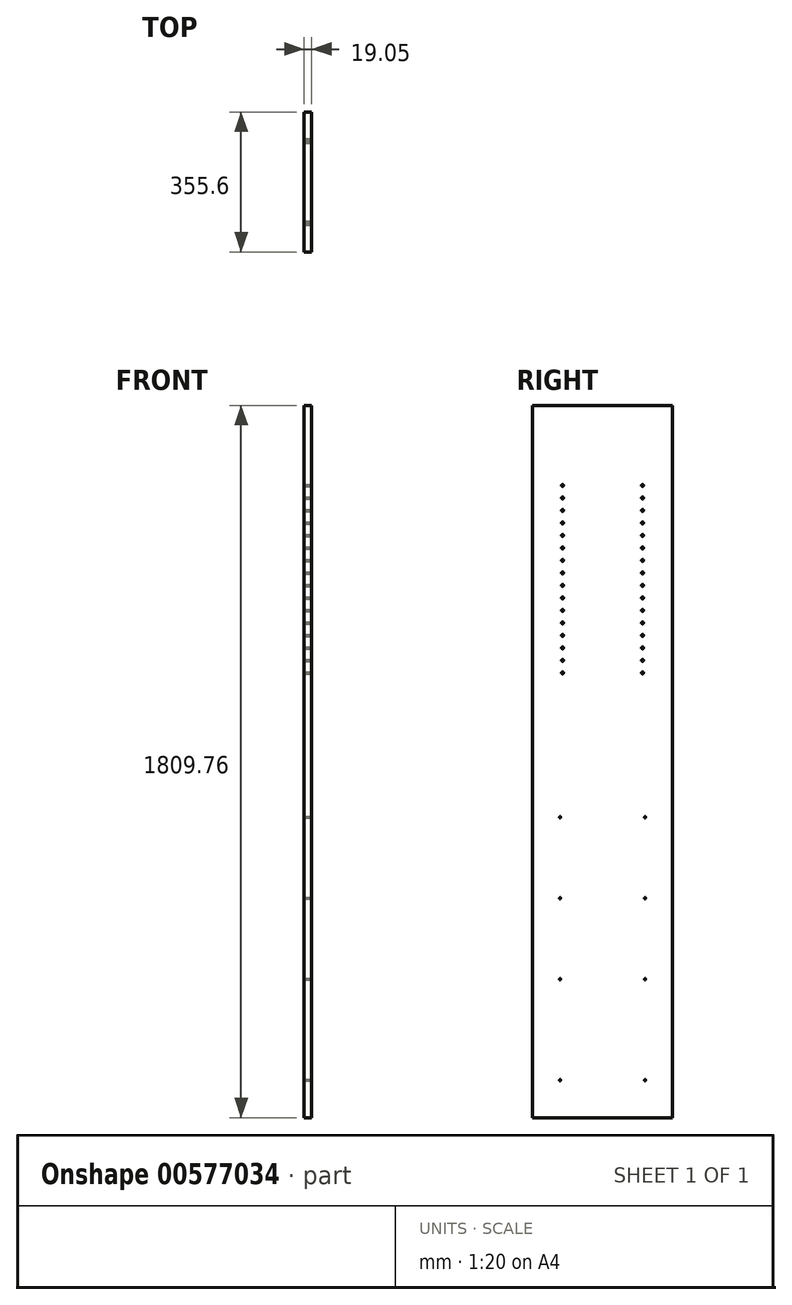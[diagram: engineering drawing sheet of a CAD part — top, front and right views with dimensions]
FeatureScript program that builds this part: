
annotation { "Feature Type Name" : "Feature", "Feature Type Description" : "" }
export const myFeature = defineFeature(function(context is Context, id is Id, definition is map)
    precondition{}
    {
        {
            var Q0;
            Q0=qCreatedBy(makeId("Right.planeOp"),FACE);
            var sketch = newSketch(context, id + "F0", { "sketchPlane" : qUnion([Q0])});
            skLineSegment(sketch, "E0.bottom", {"start": v(177.8, 904.88) * mm, "end": v(-177.8, 904.88) * mm});
            skLineSegment(sketch, "E0.top", {"start": v(177.8, -904.88) * mm, "end": v(-177.8, -904.88) * mm});
            skLineSegment(sketch, "E0.left", {"start": v(177.8, 904.88) * mm, "end": v(177.8, -904.88) * mm});
            skLineSegment(sketch, "E0.right", {"start": v(-177.8, 904.88) * mm, "end": v(-177.8, -904.88) * mm});
            skPoint(sketch, "E0.middle", {"position": v(0, 0) * mm});
            skSolve(sketch);
        }
        {
            var Q0;
            Q0=makeQuery(id+"F0.imprint","IMPRINT",FACE,{"disambiguationData":[TD([[makeQuery(id+"F0.imprint","IMPRINT",EDGE,{"derivedFrom":sQuery(id+"F0.wireOp",EDGE,"E0.bottom")}),1.0]])]});
            extrude(context, id + "F1", {"entities" : qUnion([Q0]), "depth" : 19.05 * mm, "offsetDistance" : 25.4 * mm});
        }
        {
            var Q0;
            Q0=makeQuery(id+"F1.opExtrude","CAP_FACE",FACE,{"disambiguationData":[OSD([sQuery(id+"F0.wireOp",EDGE,"E0.bottom"),sQuery(id+"F0.wireOp",EDGE,"E0.top"),sQuery(id+"F0.wireOp",EDGE,"E0.left"),sQuery(id+"F0.wireOp",EDGE,"E0.right")])],"isStart":false});
            var sketch = newSketch(context, id + "F2", { "sketchPlane" : qUnion([Q0])});
            skLineSegment(sketch, "E1", {"start": v(0, -904.88) * mm, "end": v(0, 9.53) * mm});
            skPoint(sketch, "E1.endSnap0", {"position": v(0, -904.88) * mm});
            skLineSegment(sketch, "E2", {"start": v(0, 904.88) * mm, "end": v(0, 669.92) * mm});
            skLineSegment(sketch, "E3.bottom", {"start": v(101.6, 701.68) * mm, "end": v(-101.6, 701.68) * mm});
            skLineSegment(sketch, "E3.top", {"start": v(101.6, 638.18) * mm, "end": v(-101.6, 638.18) * mm});
            skLineSegment(sketch, "E3.left", {"start": v(101.6, 701.68) * mm, "end": v(101.6, 638.18) * mm});
            skLineSegment(sketch, "E3.right", {"start": v(-101.6, 701.68) * mm, "end": v(-101.6, 638.18) * mm});
            skPoint(sketch, "E3.middle", {"position": v(0, 669.92) * mm});
            skLineSegment(sketch, "E4", {"start": v(0, 638.18) * mm, "end": v(0, 574.68) * mm});
            skLineSegment(sketch, "E5.bottom", {"start": v(-101.6, 542.93) * mm, "end": v(101.6, 542.93) * mm});
            skLineSegment(sketch, "E5.top", {"start": v(-101.6, 606.43) * mm, "end": v(101.6, 606.43) * mm});
            skLineSegment(sketch, "E5.left", {"start": v(-101.6, 542.93) * mm, "end": v(-101.6, 606.43) * mm});
            skLineSegment(sketch, "E5.right", {"start": v(101.6, 542.93) * mm, "end": v(101.6, 606.43) * mm});
            skPoint(sketch, "E5.middle", {"position": v(0, 574.68) * mm});
            skLineSegment(sketch, "E6", {"start": v(0, 542.93) * mm, "end": v(0, 479.43) * mm});
            skLineSegment(sketch, "E7.bottom", {"start": v(101.6, 447.68) * mm, "end": v(-101.6, 447.68) * mm});
            skLineSegment(sketch, "E7.top", {"start": v(101.6, 511.18) * mm, "end": v(-101.6, 511.18) * mm});
            skLineSegment(sketch, "E7.left", {"start": v(101.6, 447.68) * mm, "end": v(101.6, 511.18) * mm});
            skLineSegment(sketch, "E7.right", {"start": v(-101.6, 447.68) * mm, "end": v(-101.6, 511.18) * mm});
            skPoint(sketch, "E7.middle", {"position": v(0, 479.43) * mm});
            skLineSegment(sketch, "E8", {"start": v(0, 447.68) * mm, "end": v(0, 384.18) * mm});
            skLineSegment(sketch, "E9.bottom", {"start": v(101.6, 352.43) * mm, "end": v(-101.6, 352.43) * mm});
            skLineSegment(sketch, "E9.top", {"start": v(101.6, 415.93) * mm, "end": v(-101.6, 415.93) * mm});
            skLineSegment(sketch, "E9.left", {"start": v(101.6, 352.43) * mm, "end": v(101.6, 415.93) * mm});
            skLineSegment(sketch, "E9.right", {"start": v(-101.6, 352.43) * mm, "end": v(-101.6, 415.93) * mm});
            skPoint(sketch, "E9.middle", {"position": v(0, 384.18) * mm});
            skLineSegment(sketch, "E10", {"start": v(0, 352.43) * mm, "end": v(0, 288.93) * mm});
            skLineSegment(sketch, "E11.bottom", {"start": v(-101.6, 257.18) * mm, "end": v(101.6, 257.18) * mm});
            skLineSegment(sketch, "E11.top", {"start": v(-101.6, 320.68) * mm, "end": v(101.6, 320.68) * mm});
            skLineSegment(sketch, "E11.left", {"start": v(-101.6, 257.18) * mm, "end": v(-101.6, 320.68) * mm});
            skLineSegment(sketch, "E11.right", {"start": v(101.6, 257.18) * mm, "end": v(101.6, 320.68) * mm});
            skPoint(sketch, "E11.middle", {"position": v(0, 288.93) * mm});
            skLineSegment(sketch, "E12", {"start": v(101.6, 257.18) * mm, "end": v(101.6, 225.43) * mm});
            skLineSegment(sketch, "E13", {"start": v(-101.6, 257.18) * mm, "end": v(-101.6, 225.43) * mm});
            skPoint(sketch, "E14", {"position": v(-101.6, 701.68) * mm});
            skPoint(sketch, "E15", {"position": v(-101.6, 669.93) * mm});
            skPoint(sketch, "E16", {"position": v(-101.6, 638.18) * mm});
            skPoint(sketch, "E17", {"position": v(-101.6, 606.43) * mm});
            skPoint(sketch, "E18", {"position": v(-101.6, 574.68) * mm});
            skPoint(sketch, "E19", {"position": v(-101.6, 542.93) * mm});
            skPoint(sketch, "E20", {"position": v(-101.6, 511.18) * mm});
            skPoint(sketch, "E21", {"position": v(-101.6, 479.43) * mm});
            skPoint(sketch, "E22", {"position": v(-101.6, 447.68) * mm});
            skPoint(sketch, "E23", {"position": v(-101.6, 415.93) * mm});
            skPoint(sketch, "E24", {"position": v(-101.6, 384.18) * mm});
            skPoint(sketch, "E25", {"position": v(-101.6, 352.43) * mm});
            skPoint(sketch, "E26", {"position": v(-101.6, 320.68) * mm});
            skPoint(sketch, "E27", {"position": v(-101.6, 288.93) * mm});
            skPoint(sketch, "E28", {"position": v(-101.6, 257.18) * mm});
            skPoint(sketch, "E29", {"position": v(-101.6, 225.43) * mm});
            skPoint(sketch, "E30", {"position": v(101.6, 225.43) * mm});
            skPoint(sketch, "E31", {"position": v(101.6, 257.18) * mm});
            skPoint(sketch, "E32", {"position": v(101.6, 288.93) * mm});
            skPoint(sketch, "E33", {"position": v(101.6, 320.68) * mm});
            skPoint(sketch, "E34", {"position": v(101.6, 352.43) * mm});
            skPoint(sketch, "E35", {"position": v(101.6, 384.18) * mm});
            skPoint(sketch, "E36", {"position": v(101.6, 415.93) * mm});
            skPoint(sketch, "E37", {"position": v(101.6, 447.68) * mm});
            skPoint(sketch, "E38", {"position": v(101.6, 479.43) * mm});
            skPoint(sketch, "E39", {"position": v(101.6, 511.18) * mm});
            skPoint(sketch, "E40", {"position": v(101.6, 542.93) * mm});
            skPoint(sketch, "E41", {"position": v(101.6, 574.68) * mm});
            skPoint(sketch, "E42", {"position": v(101.6, 606.43) * mm});
            skPoint(sketch, "E43", {"position": v(101.6, 638.18) * mm});
            skPoint(sketch, "E44", {"position": v(101.6, 669.93) * mm});
            skPoint(sketch, "E45", {"position": v(101.6, 701.68) * mm});
            skSolve(sketch);
        }
        {
            var Q0;
            Q0=sQuery(id+"F2.wireOp",VERTEX,"E14");
            var Q1;
            Q1=sQuery(id+"F2.wireOp",VERTEX,"E15");
            var Q2;
            Q2=sQuery(id+"F2.wireOp",VERTEX,"E16");
            var Q3;
            Q3=sQuery(id+"F2.wireOp",VERTEX,"E17");
            var Q4;
            Q4=sQuery(id+"F2.wireOp",VERTEX,"E18");
            var Q5;
            Q5=sQuery(id+"F2.wireOp",VERTEX,"E19");
            var Q6;
            Q6=sQuery(id+"F2.wireOp",VERTEX,"E20");
            var Q7;
            Q7=sQuery(id+"F2.wireOp",VERTEX,"E21");
            var Q8;
            Q8=sQuery(id+"F2.wireOp",VERTEX,"E22");
            var Q9;
            Q9=sQuery(id+"F2.wireOp",VERTEX,"E23");
            var Q10;
            Q10=sQuery(id+"F2.wireOp",VERTEX,"E24");
            var Q11;
            Q11=sQuery(id+"F2.wireOp",VERTEX,"E25");
            var Q12;
            Q12=sQuery(id+"F2.wireOp",VERTEX,"E26");
            var Q13;
            Q13=sQuery(id+"F2.wireOp",VERTEX,"E27");
            var Q14;
            Q14=sQuery(id+"F2.wireOp",VERTEX,"E28");
            var Q15;
            Q15=sQuery(id+"F2.wireOp",VERTEX,"E29");
            var Q16;
            Q16=sQuery(id+"F2.wireOp",VERTEX,"E30");
            var Q17;
            Q17=sQuery(id+"F2.wireOp",VERTEX,"E31");
            var Q18;
            Q18=sQuery(id+"F2.wireOp",VERTEX,"E32");
            var Q19;
            Q19=sQuery(id+"F2.wireOp",VERTEX,"E33");
            var Q20;
            Q20=sQuery(id+"F2.wireOp",VERTEX,"E34");
            var Q21;
            Q21=sQuery(id+"F2.wireOp",VERTEX,"E35");
            var Q22;
            Q22=sQuery(id+"F2.wireOp",VERTEX,"E36");
            var Q23;
            Q23=sQuery(id+"F2.wireOp",VERTEX,"E37");
            var Q24;
            Q24=sQuery(id+"F2.wireOp",VERTEX,"E38");
            var Q25;
            Q25=sQuery(id+"F2.wireOp",VERTEX,"E39");
            var Q26;
            Q26=sQuery(id+"F2.wireOp",VERTEX,"E40");
            var Q27;
            Q27=sQuery(id+"F2.wireOp",VERTEX,"E41");
            var Q28;
            Q28=sQuery(id+"F2.wireOp",VERTEX,"E42");
            var Q29;
            Q29=sQuery(id+"F2.wireOp",VERTEX,"E43");
            var Q30;
            Q30=sQuery(id+"F2.wireOp",VERTEX,"E44");
            var Q31;
            Q31=sQuery(id+"F2.wireOp",VERTEX,"E45");
            var Q32;
            Q32=makeQuery(id+"F1.opExtrude","SWEPT_BODY",BODY,{"disambiguationData":[OSD([sQuery(id+"F0.wireOp",EDGE,"E0.bottom"),sQuery(id+"F0.wireOp",EDGE,"E0.top"),sQuery(id+"F0.wireOp",EDGE,"E0.left"),sQuery(id+"F0.wireOp",EDGE,"E0.right")])]});
            hole(context, id + "F3", {"style" : HoleStyle.SIMPLE, "endStyle" : HoleEndStyle.BLIND, "holeDiameter" : 5 * mm, "majorDiameter" : 6.35 * mm, "holeDepth" : 14.22 * mm, "isTappedThrough" : true, "tappedDepth" : 12.7 * mm, "tapClearance" : 3, "startFromSketch" : true, "locations" : qUnion([Q0, Q1, Q2, Q3, Q4, Q5, Q6, Q7, Q8, Q9, Q10, Q11, Q12, Q13, Q14, Q15, Q16, Q17, Q18, Q19, Q20, Q21, Q22, Q23, Q24, Q25, Q26, Q27, Q28, Q29, Q30, Q31]), "scope" : qUnion([Q32])});
        }
        {
            var Q0;
            Q0=makeQuery(id+"F1.opExtrude","CAP_FACE",FACE,{"disambiguationData":[OSD([sQuery(id+"F0.wireOp",EDGE,"E0.bottom"),sQuery(id+"F0.wireOp",EDGE,"E0.top"),sQuery(id+"F0.wireOp",EDGE,"E0.left"),sQuery(id+"F0.wireOp",EDGE,"E0.right")])],"isStart":false});
            var sketch = newSketch(context, id + "F4", { "sketchPlane" : qUnion([Q0])});
            skLineSegment(sketch, "E46.bottom", {"start": v(-177.8, -904.88) * mm, "end": v(177.8, -904.88) * mm});
            skLineSegment(sketch, "E46.top", {"start": v(-177.8, -885.83) * mm, "end": v(177.8, -885.83) * mm});
            skLineSegment(sketch, "E46.left", {"start": v(-177.8, -904.88) * mm, "end": v(-177.8, -885.83) * mm});
            skLineSegment(sketch, "E46.right", {"start": v(177.8, -904.88) * mm, "end": v(177.8, -885.83) * mm});
            skLineSegment(sketch, "E47", {"start": v(0, -885.83) * mm, "end": v(0, -828.68) * mm});
            skLineSegment(sketch, "E48", {"start": v(-177.8, -809.62) * mm, "end": v(-107.95, -809.62) * mm});
            skLineSegment(sketch, "E49", {"start": v(177.8, -809.62) * mm, "end": v(107.95, -809.62) * mm});
            skLineSegment(sketch, "E50.bottom", {"start": v(-177.8, -885.83) * mm, "end": v(-196.85, -885.83) * mm});
            skLineSegment(sketch, "E50.top", {"start": v(-177.8, -631.83) * mm, "end": v(-196.85, -631.83) * mm});
            skLineSegment(sketch, "E50.left", {"start": v(-177.8, -885.83) * mm, "end": v(-177.8, -631.83) * mm});
            skLineSegment(sketch, "E50.right", {"start": v(-196.85, -885.83) * mm, "end": v(-196.85, -631.83) * mm});
            skLineSegment(sketch, "E51", {"start": v(-196.85, -631.83) * mm, "end": v(-196.85, -629.29) * mm});
            skLineSegment(sketch, "E52.bottom", {"start": v(-196.85, -629.29) * mm, "end": v(-177.8, -629.29) * mm});
            skLineSegment(sketch, "E52.top", {"start": v(-196.85, -426.09) * mm, "end": v(-177.8, -426.09) * mm});
            skLineSegment(sketch, "E52.left", {"start": v(-196.85, -629.29) * mm, "end": v(-196.85, -426.09) * mm});
            skLineSegment(sketch, "E52.right", {"start": v(-177.8, -629.29) * mm, "end": v(-177.8, -426.09) * mm});
            skLineSegment(sketch, "E53", {"start": v(0, -885.83) * mm, "end": v(0, -9.53) * mm});
            skLineSegment(sketch, "E54", {"start": v(-196.85, -426.09) * mm, "end": v(-196.85, -423.55) * mm});
            skLineSegment(sketch, "E55.bottom", {"start": v(-196.85, -423.55) * mm, "end": v(-177.8, -423.55) * mm});
            skLineSegment(sketch, "E55.top", {"start": v(-196.85, -220.35) * mm, "end": v(-177.8, -220.35) * mm});
            skLineSegment(sketch, "E55.left", {"start": v(-196.85, -423.55) * mm, "end": v(-196.85, -220.35) * mm});
            skLineSegment(sketch, "E55.right", {"start": v(-177.8, -423.55) * mm, "end": v(-177.8, -220.35) * mm});
            skLineSegment(sketch, "E56", {"start": v(0, -9.53) * mm, "end": v(-177.8, -9.53) * mm});
            skLineSegment(sketch, "E57", {"start": v(-196.85, -220.35) * mm, "end": v(-196.85, -217.8) * mm});
            skLineSegment(sketch, "E58.bottom", {"start": v(-196.85, -217.8) * mm, "end": v(-177.8, -217.8) * mm});
            skLineSegment(sketch, "E58.top", {"start": v(-196.85, -14.6) * mm, "end": v(-177.8, -14.6) * mm});
            skLineSegment(sketch, "E58.left", {"start": v(-196.85, -217.8) * mm, "end": v(-196.85, -14.6) * mm});
            skLineSegment(sketch, "E58.right", {"start": v(-177.8, -217.8) * mm, "end": v(-177.8, -14.6) * mm});
            skLineSegment(sketch, "E59", {"start": v(-177.8, -629.29) * mm, "end": v(-177.8, -553.09) * mm});
            skLineSegment(sketch, "E60", {"start": v(-177.8, -553.09) * mm, "end": v(-107.95, -553.09) * mm});
            skLineSegment(sketch, "E61", {"start": v(-177.8, -423.55) * mm, "end": v(-177.8, -347.35) * mm});
            skLineSegment(sketch, "E62", {"start": v(-177.8, -347.35) * mm, "end": v(-107.95, -347.35) * mm});
            skLineSegment(sketch, "E63", {"start": v(-177.8, -885.83) * mm, "end": v(-177.8, -809.62) * mm});
            skLineSegment(sketch, "E64", {"start": v(177.8, -885.83) * mm, "end": v(177.8, -809.62) * mm});
            skLineSegment(sketch, "E65", {"start": v(-177.8, -217.8) * mm, "end": v(-177.8, -141.6) * mm});
            skLineSegment(sketch, "E66", {"start": v(-177.8, -141.6) * mm, "end": v(-107.95, -141.6) * mm});
            skLineSegment(sketch, "E67", {"start": v(107.95, -809.62) * mm, "end": v(107.95, -553.09) * mm});
            skLineSegment(sketch, "E68", {"start": v(107.95, -553.09) * mm, "end": v(107.95, -347.35) * mm});
            skLineSegment(sketch, "E69", {"start": v(107.95, -347.35) * mm, "end": v(107.95, -141.6) * mm});
            skPoint(sketch, "E70", {"position": v(-107.95, -141.6) * mm});
            skPoint(sketch, "E71", {"position": v(107.95, -141.6) * mm});
            skPoint(sketch, "E72", {"position": v(107.95, -347.35) * mm});
            skPoint(sketch, "E73", {"position": v(-107.95, -347.35) * mm});
            skPoint(sketch, "E74", {"position": v(-107.95, -553.09) * mm});
            skPoint(sketch, "E75", {"position": v(107.95, -553.09) * mm});
            skPoint(sketch, "E76", {"position": v(-107.95, -809.62) * mm});
            skPoint(sketch, "E77", {"position": v(107.95, -809.62) * mm});
            skSolve(sketch);
        }
        {
            var Q0;
            Q0=sQuery(id+"F4.wireOp",VERTEX,"E70");
            var Q1;
            Q1=sQuery(id+"F4.wireOp",VERTEX,"E71");
            var Q2;
            Q2=sQuery(id+"F4.wireOp",VERTEX,"E72");
            var Q3;
            Q3=sQuery(id+"F4.wireOp",VERTEX,"E73");
            var Q4;
            Q4=sQuery(id+"F4.wireOp",VERTEX,"E74");
            var Q5;
            Q5=sQuery(id+"F4.wireOp",VERTEX,"E75");
            var Q6;
            Q6=sQuery(id+"F4.wireOp",VERTEX,"E77");
            var Q7;
            Q7=sQuery(id+"F4.wireOp",VERTEX,"E76");
            var Q8;
            Q8=makeQuery(id+"F1.opExtrude","SWEPT_BODY",BODY,{"disambiguationData":[OSD([sQuery(id+"F0.wireOp",EDGE,"E0.bottom"),sQuery(id+"F0.wireOp",EDGE,"E0.top"),sQuery(id+"F0.wireOp",EDGE,"E0.left"),sQuery(id+"F0.wireOp",EDGE,"E0.right")])]});
            hole(context, id + "F5", {"style" : HoleStyle.SIMPLE, "endStyle" : HoleEndStyle.BLIND, "holeDiameter" : 3.17 * mm, "majorDiameter" : 6.35 * mm, "holeDepth" : 14.22 * mm, "isTappedThrough" : true, "tappedDepth" : 12.7 * mm, "tapClearance" : 3, "startFromSketch" : true, "locations" : qUnion([Q0, Q1, Q2, Q3, Q4, Q5, Q6, Q7]), "scope" : qUnion([Q8])});
        }
    });
